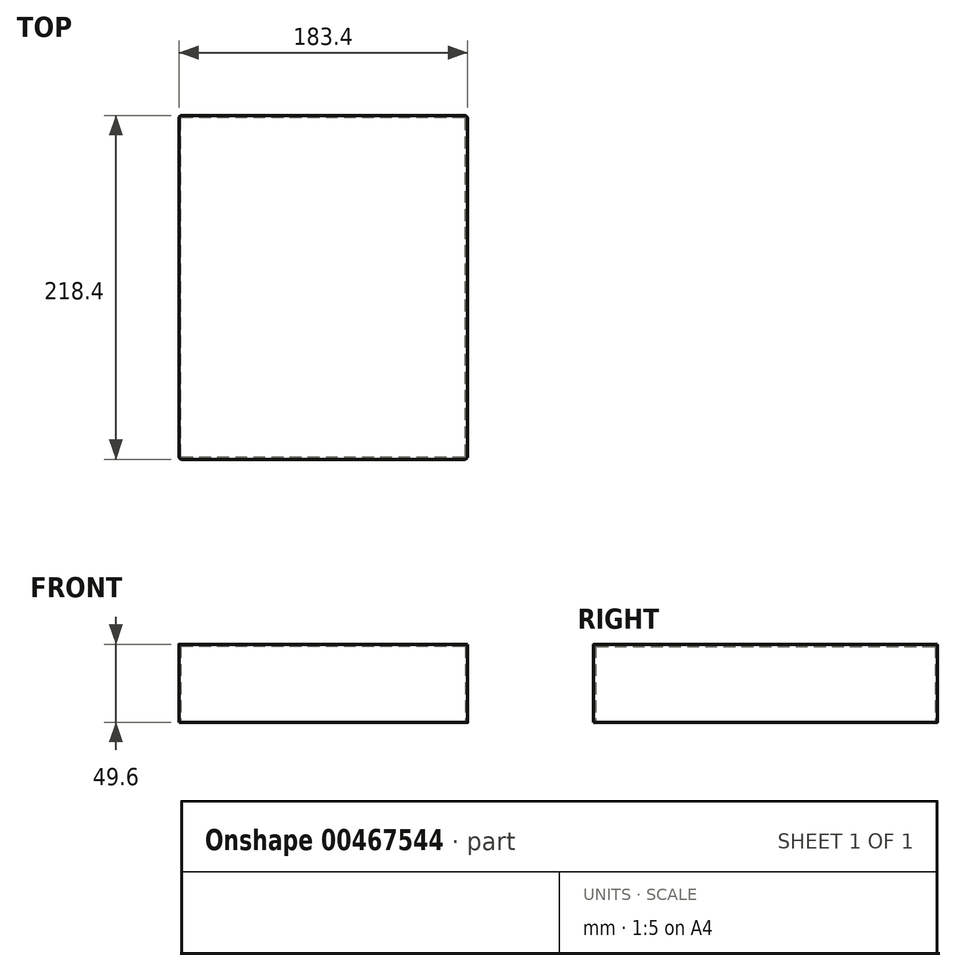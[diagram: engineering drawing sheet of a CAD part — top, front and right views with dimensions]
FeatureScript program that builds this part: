
annotation { "Feature Type Name" : "Feature", "Feature Type Description" : "" }
export const myFeature = defineFeature(function(context is Context, id is Id, definition is map)
    precondition{}
    {
        {
            var Q0;
            Q0=qCreatedBy(makeId("Top.planeOp"),FACE);
            var sketch = newSketch(context, id + "F0", { "sketchPlane" : qUnion([Q0])});
            skLineSegment(sketch, "E0.bottom", {"start": v(91.7, -109.2) * mm, "end": v(-91.7, -109.2) * mm});
            skLineSegment(sketch, "E0.top", {"start": v(91.7, 109.2) * mm, "end": v(-91.7, 109.2) * mm});
            skLineSegment(sketch, "E0.left", {"start": v(91.7, -109.2) * mm, "end": v(91.7, 109.2) * mm});
            skLineSegment(sketch, "E0.right", {"start": v(-91.7, -109.2) * mm, "end": v(-91.7, 109.2) * mm});
            skPoint(sketch, "E0.middle", {"position": v(0, 0) * mm});
            skSolve(sketch);
        }
        {
            var Q0;
            Q0 = qSketchRegion(id + "F0", true);
            extrude(context, id + "F1", {"entities" : qUnion([Q0]), "depth" : (45 + 2 * 1.2 + 2 * 2.1 - 2) * mm});
        }
        {
            var Q0;
            Q0=makeQuery(id+"F1.opExtrude","CAP_FACE",FACE,{"disambiguationData":[OSD([sQuery(id+"F0.wireOp",EDGE,"E0.bottom"),sQuery(id+"F0.wireOp",EDGE,"E0.top"),sQuery(id+"F0.wireOp",EDGE,"E0.left"),sQuery(id+"F0.wireOp",EDGE,"E0.right")])],"isStart":true});
            shell(context, id + "F2", {"entities" : qUnion([Q0]), "thickness" : 1.2 * mm});
        }
        {
            var Q0;
            Q0=makeQuery(id+"F1.opExtrude","SWEPT_EDGE",EDGE,{"disambiguationData":[OSD([sQuery(id+"F0.wireOp",EDGE,"E0.bottom"),sQuery(id+"F0.wireOp",EDGE,"E0.right")])]});
            var Q1;
            Q1=makeQuery(id+"F1.opExtrude","SWEPT_EDGE",EDGE,{"disambiguationData":[OSD([sQuery(id+"F0.wireOp",EDGE,"E0.top"),sQuery(id+"F0.wireOp",EDGE,"E0.right")])]});
            var Q2;
            Q2=makeQuery(id+"F1.opExtrude","SWEPT_EDGE",EDGE,{"disambiguationData":[OSD([sQuery(id+"F0.wireOp",EDGE,"E0.top"),sQuery(id+"F0.wireOp",EDGE,"E0.left")])]});
            var Q3;
            Q3=makeQuery(id+"F1.opExtrude","SWEPT_EDGE",EDGE,{"disambiguationData":[OSD([sQuery(id+"F0.wireOp",EDGE,"E0.bottom"),sQuery(id+"F0.wireOp",EDGE,"E0.left")])]});
            fillet(context, id + "F3", {"entities" : qUnion([Q0, Q1, Q2, Q3]), "radius" : 2 * mm, "tangentPropagation" : true, "allowEdgeOverflow" : false});
        }
        {
            var Q0;
            Q0=makeQuery(id+"F2.opShell","OFFSET_EDGE",EDGE,{"disambiguationData":[OSD([sQuery(id+"F0.wireOp",EDGE,"E0.bottom"),sQuery(id+"F0.wireOp",EDGE,"E0.right")])]});
            var Q1;
            Q1=makeQuery(id+"F2.opShell","OFFSET_EDGE",EDGE,{"disambiguationData":[OSD([sQuery(id+"F0.wireOp",EDGE,"E0.bottom"),sQuery(id+"F0.wireOp",EDGE,"E0.left")])]});
            var Q2;
            Q2=makeQuery(id+"F2.opShell","OFFSET_EDGE",EDGE,{"disambiguationData":[OSD([sQuery(id+"F0.wireOp",EDGE,"E0.top"),sQuery(id+"F0.wireOp",EDGE,"E0.left")])]});
            var Q3;
            Q3=makeQuery(id+"F2.opShell","OFFSET_EDGE",EDGE,{"disambiguationData":[OSD([sQuery(id+"F0.wireOp",EDGE,"E0.top"),sQuery(id+"F0.wireOp",EDGE,"E0.right")])]});
            fillet(context, id + "F4", {"entities" : qUnion([Q0, Q1, Q2, Q3]), "radius" : .8 * mm, "tangentPropagation" : true, "allowEdgeOverflow" : false});
        }
    });
